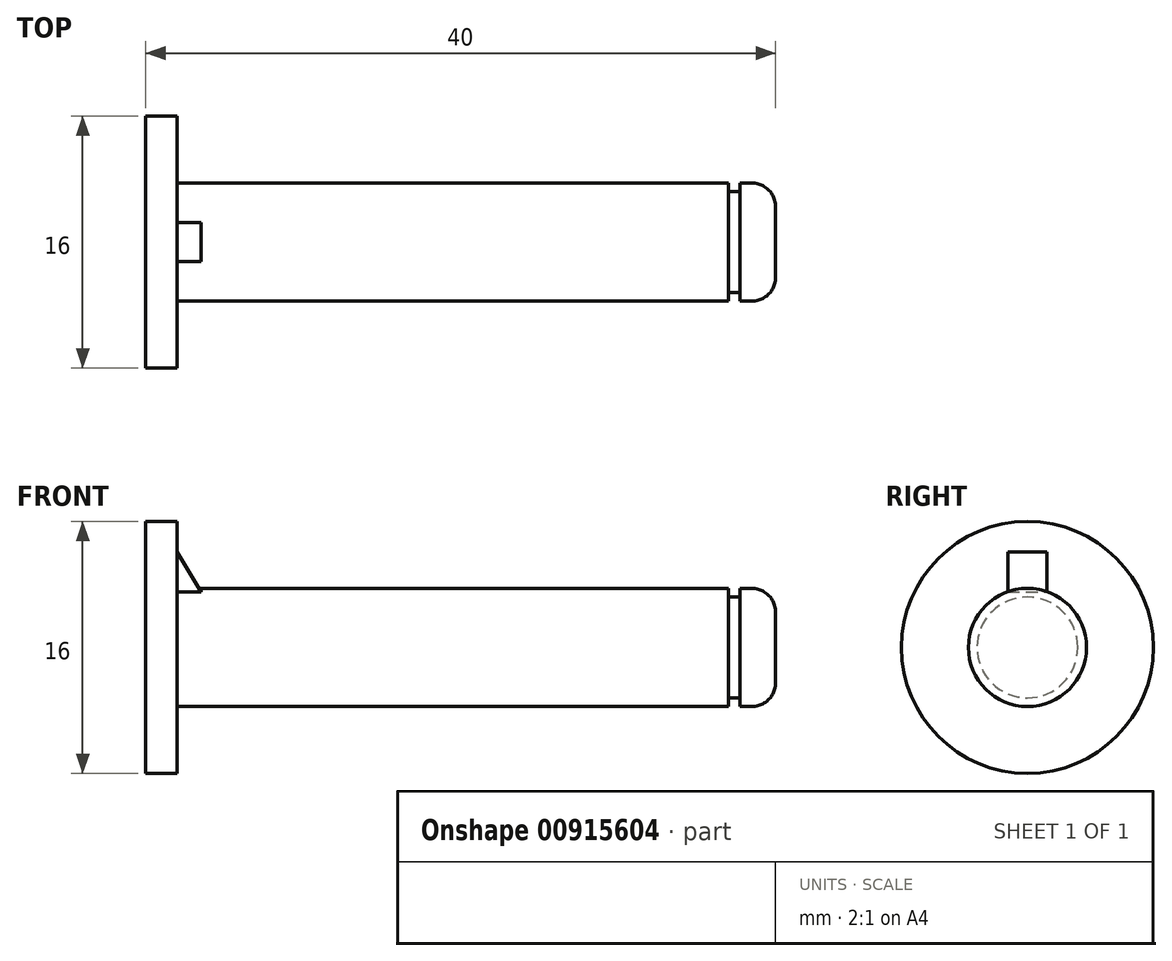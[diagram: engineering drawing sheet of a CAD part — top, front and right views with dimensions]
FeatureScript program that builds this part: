
annotation { "Feature Type Name" : "Feature", "Feature Type Description" : "" }
export const myFeature = defineFeature(function(context is Context, id is Id, definition is map)
    precondition{}
    {
        {
            var Q0;
            Q0=qCreatedBy(makeId("Front.planeOp"),FACE);
            var sketch = newSketch(context, id + "F0", { "sketchPlane" : qUnion([Q0])});
            skLineSegment(sketch, "E0", {"start": v(0, 0) * mm, "end": v(0, 8) * mm});
            skLineSegment(sketch, "E1", {"start": v(0, 8) * mm, "end": v(2, 8) * mm});
            skLineSegment(sketch, "E2", {"start": v(2, 8) * mm, "end": v(2, 3.75) * mm});
            skLineSegment(sketch, "E3", {"start": v(2, 3.75) * mm, "end": v(37, 3.75) * mm});
            skLineSegment(sketch, "E4", {"start": v(37, 3.75) * mm, "end": v(37, 3.2) * mm});
            skLineSegment(sketch, "E5", {"start": v(37, 3.2) * mm, "end": v(37.73, 3.2) * mm});
            skLineSegment(sketch, "E6", {"start": v(37.73, 3.2) * mm, "end": v(37.73, 3.75) * mm});
            skLineSegment(sketch, "E7", {"start": v(37.73, 3.75) * mm, "end": v(40, 3.75) * mm});
            skLineSegment(sketch, "E8", {"start": v(40, 3.75) * mm, "end": v(40, 0) * mm});
            skLineSegment(sketch, "E9", {"start": v(40, 0) * mm, "end": v(0, 0) * mm});
            skSolve(sketch);
        }
        {
            var Q0;
            Q0=makeQuery(id+"F0.imprint","IMPRINT",FACE,{"disambiguationData":[TD([[makeQuery(id+"F0.imprint","IMPRINT",EDGE,{"derivedFrom":sQuery(id+"F0.wireOp",EDGE,"E0")}),-1.0]])]});
            var Q1;
            Q1=sQuery(id+"F0.wireOp",EDGE,"E9");
            revolve(context, id + "F1", {"surfaceOperationType" : NewSurfaceOperationType.NEW, "entities" : qUnion([Q0]), "axis" : qUnion([Q1]), "revolveType" : RevolveType.FULL});
        }
        {
            var Q0;
            Q0=makeQuery(id+"F1.opRevolve","SWEPT_FACE",FACE,{"disambiguationData":[OSD([sQuery(id+"F0.wireOp",EDGE,"E2")])]});
            var sketch = newSketch(context, id + "F2", { "sketchPlane" : qUnion([Q0])});
            skLineSegment(sketch, "E10", {"start": v(-1.25, 3.54) * mm, "end": v(-1.25, 6.08) * mm});
            skLineSegment(sketch, "E11", {"start": v(-1.25, 6.08) * mm, "end": v(1.25, 6.08) * mm});
            skLineSegment(sketch, "E12", {"start": v(1.25, 6.08) * mm, "end": v(1.25, 3.54) * mm});
            skSolve(sketch);
        }
        {
            var Q0;
            Q0 = qSketchRegion(id + "F2", true);
            var Q1;
            {var subQ0=sQuery(id+"F2.wireOp",EDGE,"E10");Q1=makeQuery(id+"F2.imprint","IMPRINT",FACE,{"disambiguationData":[TD([[makeQuery(id+"F2.imprint","IMPRINT",EDGE,{"derivedFrom":subQ0}),-1.0]])]});}
            extrude(context, id + "F3", {"entities" : qUnion([Q0, Q1]), "operationType" : NewBodyOperationType.ADD, "endBound" : BoundingType.SYMMETRIC, "depth" : 3 * mm, "offsetDistance" : 25 * mm});
        }
        {
            var Q0;
            Q0=makeQuery(id+"F3.opExtrude","SWEPT_FACE",FACE,{"disambiguationData":[OSD([sQuery(id+"F2.wireOp",EDGE,"E12")])]});
            var sketch = newSketch(context, id + "F4", { "sketchPlane" : qUnion([Q0])});
            skLineSegment(sketch, "E13", {"start": v(-2, 6.08) * mm, "end": v(-3.5, 3.54) * mm});
            skSolve(sketch);
        }
        {
            var Q0;
            Q0=makeQuery(id+"F4.imprint","IMPRINT",FACE,{"disambiguationData":[TD([[makeQuery(id+"F4.imprint","IMPRINT",EDGE,{"derivedFrom":sQuery(id+"F4.wireOp",EDGE,"E13")}),-1.0]])]});
            extrude(context, id + "F5", {"entities" : qUnion([Q0]), "operationType" : NewBodyOperationType.REMOVE, "oppositeDirection" : true, "depth" : 25 * mm, "offsetDistance" : 25 * mm});
        }
        {
            var Q0;
            Q0=makeQuery(id+"F1.opRevolve","SWEPT_EDGE",EDGE,{"disambiguationData":[OSD([sQuery(id+"F0.wireOp",EDGE,"E7"),sQuery(id+"F0.wireOp",EDGE,"E8")])]});
            fillet(context, id + "F6", {"entities" : qUnion([Q0]), "radius" : 1.5 * mm, "tangentPropagation" : true, "allowEdgeOverflow" : false});
        }
    });
